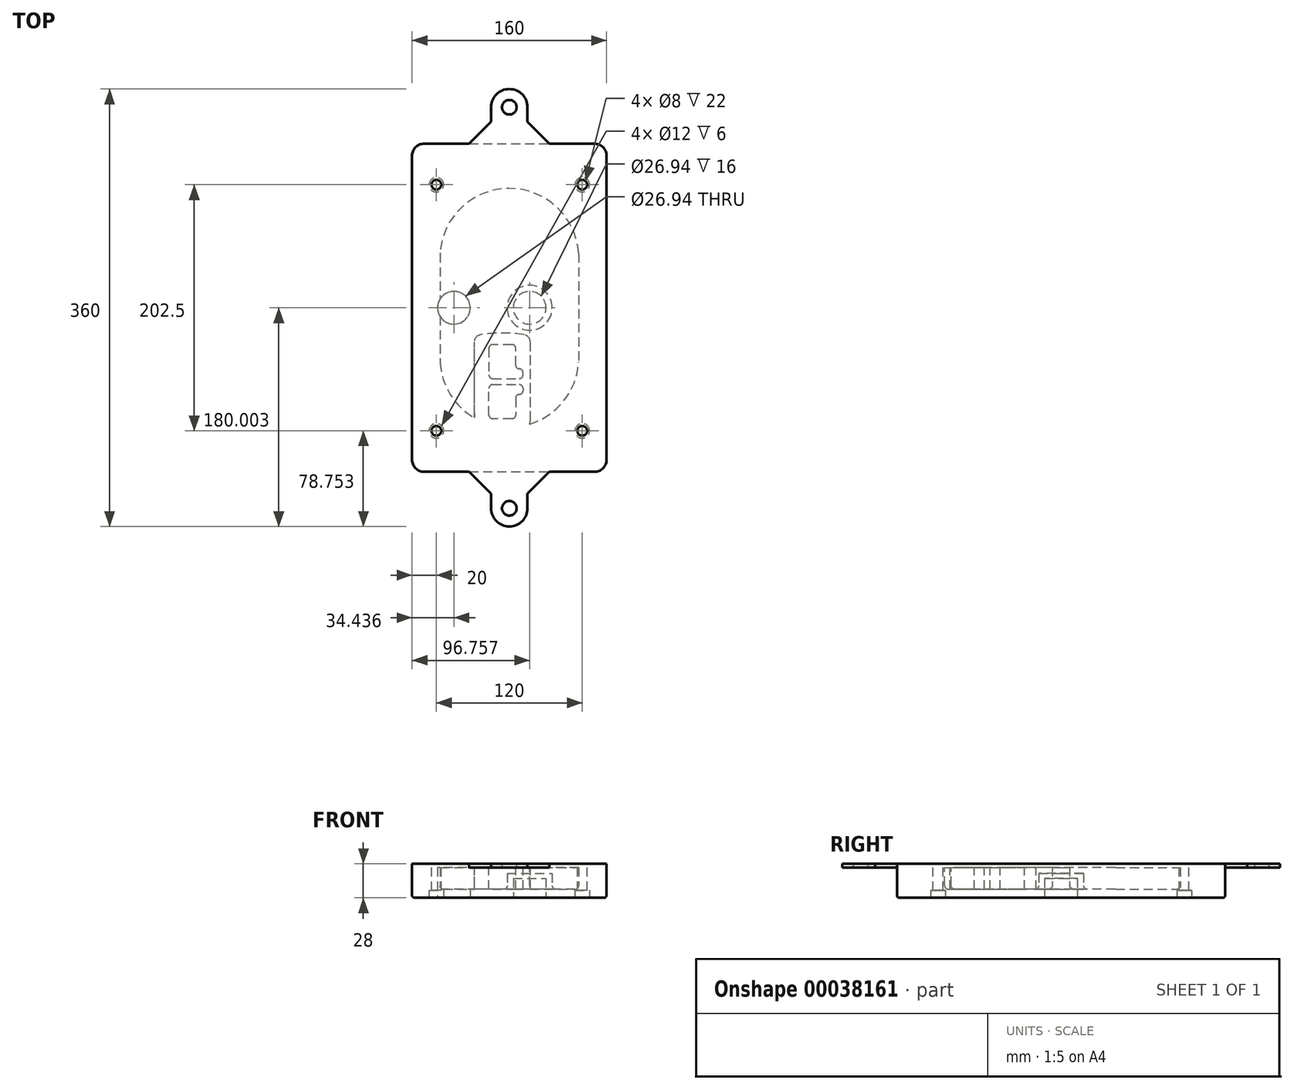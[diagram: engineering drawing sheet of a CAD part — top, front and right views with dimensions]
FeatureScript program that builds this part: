
annotation { "Feature Type Name" : "Feature", "Feature Type Description" : "" }
export const myFeature = defineFeature(function(context is Context, id is Id, definition is map)
    precondition{}
    {
        {
            var Q0;
            Q0=qCreatedBy(makeId("Top.planeOp"),FACE);
            var sketch = newSketch(context, id + "F0", { "sketchPlane" : qUnion([Q0])});
            skPoint(sketch, "E0.rect.middle", {"position": v(0, 0) * mm});
            skLineSegment(sketch, "E1.bottom", {"start": v(24.05, 28.38) * mm, "end": v(164.05, 28.38) * mm});
            skLineSegment(sketch, "E1.top", {"start": v(24.05, 298.38) * mm, "end": v(164.05, 298.38) * mm});
            skLineSegment(sketch, "E1.left", {"start": v(14.05, 38.38) * mm, "end": v(14.05, 288.38) * mm});
            skLineSegment(sketch, "E1.right", {"start": v(174.05, 38.38) * mm, "end": v(174.05, 288.38) * mm});
            skLineSegment(sketch, "E2", {"start": v(14.05, 298.38) * mm, "end": v(174.05, 28.38) * mm, "construction": true});
            skLineSegment(sketch, "E3", {"start": v(174.05, 298.38) * mm, "end": v(14.05, 28.38) * mm, "construction": true});
            skCircle(sketch, "E4", {"center": v(34.05, 264.63) * mm, "radius": 4 * mm});
            skCircle(sketch, "E5", {"center": v(154.05, 264.63) * mm, "radius": 4 * mm});
            skCircle(sketch, "E6", {"center": v(154.05, 62.13) * mm, "radius": 4 * mm});
            skCircle(sketch, "E7", {"center": v(34.05, 62.13) * mm, "radius": 4 * mm});
            skLineSegment(sketch, "E8", {"start": v(34.05, 264.63) * mm, "end": v(154.05, 264.63) * mm, "construction": true});
            skLineSegment(sketch, "E9", {"start": v(154.05, 264.63) * mm, "end": v(154.05, 62.13) * mm, "construction": true});
            skLineSegment(sketch, "E10", {"start": v(154.05, 62.13) * mm, "end": v(34.05, 62.13) * mm, "construction": true});
            skLineSegment(sketch, "E11", {"start": v(34.05, 62.13) * mm, "end": v(34.05, 264.63) * mm, "construction": true});
            skLineSegment(sketch, "E12", {"start": v(34.05, 208.05) * mm, "end": v(34.05, 118.72) * mm});
            skLineSegment(sketch, "E13", {"start": v(154.05, 208.05) * mm, "end": v(154.05, 118.72) * mm});
            skArc(sketch, "E14", {"start": v(154.03, 208.75) * mm, "mid": v(94.05, 264.63) * mm, "end": v(34.07, 208.75) * mm});
            skArc(sketch, "E15", {"start": v(34.07, 118.01) * mm, "mid": v(94.05, 62.13) * mm, "end": v(154.03, 118.01) * mm});
            skLineSegment(sketch, "E16", {"start": v(34.05, 163.38) * mm, "end": v(154.05, 163.38) * mm, "construction": true});
            skPoint(sketch, "E17.visualSharp", {"position": v(34.05, 118.38) * mm});
            skArc(sketch, "E17.filletArc", {"start": v(34.05, 118.72) * mm, "mid": v(34.06, 118.37) * mm, "end": v(34.07, 118.01) * mm});
            skPoint(sketch, "E18.visualSharp", {"position": v(34.05, 208.38) * mm});
            skArc(sketch, "E18.filletArc", {"start": v(34.07, 208.75) * mm, "mid": v(34.06, 208.4) * mm, "end": v(34.05, 208.05) * mm});
            skPoint(sketch, "E19.visualSharp", {"position": v(154.05, 208.38) * mm});
            skArc(sketch, "E19.filletArc", {"start": v(154.05, 208.05) * mm, "mid": v(154.04, 208.4) * mm, "end": v(154.03, 208.75) * mm});
            skPoint(sketch, "E20.visualSharp", {"position": v(154.05, 118.38) * mm});
            skArc(sketch, "E20.filletArc", {"start": v(154.03, 118.01) * mm, "mid": v(154.04, 118.37) * mm, "end": v(154.05, 118.72) * mm});
            skPoint(sketch, "E21.visualSharp", {"position": v(14.05, 298.38) * mm});
            skArc(sketch, "E21.filletArc", {"start": v(24.05, 298.38) * mm, "mid": v(16.98, 295.45) * mm, "end": v(14.05, 288.38) * mm});
            skPoint(sketch, "E22.visualSharp", {"position": v(174.05, 298.38) * mm});
            skArc(sketch, "E22.filletArc", {"start": v(174.05, 288.38) * mm, "mid": v(171.12, 295.45) * mm, "end": v(164.05, 298.38) * mm});
            skPoint(sketch, "E23.visualSharp", {"position": v(174.05, 28.38) * mm});
            skArc(sketch, "E23.filletArc", {"start": v(164.05, 28.38) * mm, "mid": v(171.12, 31.31) * mm, "end": v(174.05, 38.38) * mm});
            skPoint(sketch, "E24.visualSharp", {"position": v(14.05, 28.38) * mm});
            skArc(sketch, "E24.filletArc", {"start": v(14.05, 38.38) * mm, "mid": v(16.98, 31.31) * mm, "end": v(24.05, 28.38) * mm});
            skArc(sketch, "E25.0", {"start": v(151.05, 208.05) * mm, "mid": v(151.05, 208.3) * mm, "end": v(151.03, 208.54) * mm});
            skLineSegment(sketch, "E25.1", {"start": v(151.05, 208.05) * mm, "end": v(151.05, 118.72) * mm});
            skArc(sketch, "E25.2", {"start": v(151.03, 118.23) * mm, "mid": v(151.05, 118.47) * mm, "end": v(151.05, 118.72) * mm});
            skArc(sketch, "E25.3", {"start": v(37.07, 118.23) * mm, "mid": v(94.05, 65.13) * mm, "end": v(151.03, 118.23) * mm});
            skArc(sketch, "E25.4", {"start": v(37.05, 118.72) * mm, "mid": v(37.05, 118.47) * mm, "end": v(37.07, 118.23) * mm});
            skArc(sketch, "E25.5", {"start": v(151.03, 208.54) * mm, "mid": v(94.05, 261.63) * mm, "end": v(37.07, 208.54) * mm});
            skLineSegment(sketch, "E25.6", {"start": v(37.05, 208.05) * mm, "end": v(37.05, 118.72) * mm});
            skArc(sketch, "E25.7", {"start": v(37.07, 208.54) * mm, "mid": v(37.05, 208.3) * mm, "end": v(37.05, 208.05) * mm});
            skArc(sketch, "E26.0", {"start": v(30.08, 209.03) * mm, "mid": v(30.06, 208.54) * mm, "end": v(30.05, 208.05) * mm});
            skArc(sketch, "E26.1", {"start": v(158.02, 209.03) * mm, "mid": v(94.05, 268.63) * mm, "end": v(30.08, 209.03) * mm});
            skArc(sketch, "E26.2", {"start": v(158.05, 208.05) * mm, "mid": v(158.04, 208.54) * mm, "end": v(158.02, 209.03) * mm});
            skLineSegment(sketch, "E26.3", {"start": v(158.05, 208.05) * mm, "end": v(158.05, 118.72) * mm});
            skArc(sketch, "E26.4", {"start": v(158.02, 117.73) * mm, "mid": v(158.04, 118.23) * mm, "end": v(158.05, 118.72) * mm});
            skLineSegment(sketch, "E26.5", {"start": v(30.05, 208.05) * mm, "end": v(30.05, 118.72) * mm});
            skArc(sketch, "E26.6", {"start": v(30.08, 117.73) * mm, "mid": v(94.05, 58.13) * mm, "end": v(158.02, 117.73) * mm});
            skArc(sketch, "E26.7", {"start": v(30.05, 118.72) * mm, "mid": v(30.06, 118.23) * mm, "end": v(30.08, 117.73) * mm});
            skSolve(sketch);
        }
        {
            var Q0;
            Q0=makeQuery(id+"F0.imprint","IMPRINT",FACE,{"disambiguationData":[TD([[makeQuery(id+"F0.imprint","IMPRINT",EDGE,{"derivedFrom":sQuery(id+"F0.wireOp",EDGE,"E1.bottom")}),1.0]])]});
            var Q1;
            Q1=makeQuery(id+"F0.imprint","IMPRINT",FACE,{"disambiguationData":[TD([[makeQuery(id+"F0.imprint","IMPRINT",EDGE,{"derivedFrom":sQuery(id+"F0.wireOp",EDGE,"E12")}),1.0]])]});
            var Q2;
            Q2=makeQuery(id+"F0.imprint","IMPRINT",FACE,{"disambiguationData":[TD([[makeQuery(id+"F0.imprint","IMPRINT",EDGE,{"derivedFrom":sQuery(id+"F0.wireOp",EDGE,"E25.0")}),1.0]])]});
            var Q3;
            Q3=makeQuery(id+"F0.imprint","IMPRINT",FACE,{"disambiguationData":[TD([[makeQuery(id+"F0.imprint","IMPRINT",EDGE,{"derivedFrom":sQuery(id+"F0.wireOp",EDGE,"E12")}),-1.0]])]});
            extrude(context, id + "F1", {"entities" : qUnion([Q0, Q1, Q2, Q3]), "oppositeDirection" : true, "depth" : 25 * mm});
        }
        {
            var Q0;
            Q0=makeQuery(id+"F0.imprint","IMPRINT",FACE,{"disambiguationData":[TD([[makeQuery(id+"F0.imprint","IMPRINT",EDGE,{"derivedFrom":sQuery(id+"F0.wireOp",EDGE,"E12")}),1.0]])]});
            extrude(context, id + "F2", {"entities" : qUnion([Q0]), "operationType" : NewBodyOperationType.ADD, "depth" : 3 * mm});
        }
        {
            var Q0;
            Q0=makeQuery(id+"F0.imprint","IMPRINT",FACE,{"disambiguationData":[TD([[makeQuery(id+"F0.imprint","IMPRINT",EDGE,{"derivedFrom":sQuery(id+"F0.wireOp",EDGE,"E25.0")}),1.0]])]});
            extrude(context, id + "F3", {"entities" : qUnion([Q0]), "operationType" : NewBodyOperationType.REMOVE, "oppositeDirection" : true, "depth" : 18 * mm});
        }
        {
            var Q0;
            Q0=makeQuery(id+"F2.opExtrude","CAP_FACE",FACE,{"disambiguationData":[OSD([sQuery(id+"F0.wireOp",EDGE,"E12"),sQuery(id+"F0.wireOp",EDGE,"E13"),sQuery(id+"F0.wireOp",EDGE,"E14"),sQuery(id+"F0.wireOp",EDGE,"E15"),sQuery(id+"F0.wireOp",EDGE,"E17.filletArc"),sQuery(id+"F0.wireOp",EDGE,"E18.filletArc"),sQuery(id+"F0.wireOp",EDGE,"E19.filletArc"),sQuery(id+"F0.wireOp",EDGE,"E20.filletArc"),sQuery(id+"F0.wireOp",EDGE,"E25.0"),sQuery(id+"F0.wireOp",EDGE,"E25.1"),sQuery(id+"F0.wireOp",EDGE,"E25.2"),sQuery(id+"F0.wireOp",EDGE,"E25.3"),sQuery(id+"F0.wireOp",EDGE,"E25.4"),sQuery(id+"F0.wireOp",EDGE,"E25.5"),sQuery(id+"F0.wireOp",EDGE,"E25.6"),sQuery(id+"F0.wireOp",EDGE,"E25.7")])],"isStart":false});
            var sketch = newSketch(context, id + "F4", { "sketchPlane" : qUnion([Q0])});
            skArc(sketch, "E27.0", {"start": v(69.96, 62.18) * mm, "mid": v(88.3, 60.63) * mm, "end": v(106.64, 62.18) * mm});
            skArc(sketch, "E28.0", {"start": v(106.64, 143.09) * mm, "mid": v(88.3, 144.63) * mm, "end": v(69.96, 143.09) * mm});
            skLineSegment(sketch, "E29", {"start": v(63.3, 135.2) * mm, "end": v(63.3, 70.07) * mm});
            skLineSegment(sketch, "E30", {"start": v(113.3, 135.2) * mm, "end": v(113.3, 70.07) * mm});
            skLineSegment(sketch, "E31", {"start": v(63.3, 141.74) * mm, "end": v(113.3, 141.74) * mm, "construction": true});
            skLineSegment(sketch, "E32", {"start": v(63.3, 63.52) * mm, "end": v(113.3, 63.52) * mm, "construction": true});
            skPoint(sketch, "E33.visualSharp", {"position": v(63.3, 141.74) * mm});
            skArc(sketch, "E33.filletArc", {"start": v(69.96, 143.09) * mm, "mid": v(65.19, 140.36) * mm, "end": v(63.3, 135.2) * mm});
            skPoint(sketch, "E34.visualSharp", {"position": v(113.3, 141.74) * mm});
            skArc(sketch, "E34.filletArc", {"start": v(113.3, 135.2) * mm, "mid": v(111.41, 140.36) * mm, "end": v(106.64, 143.09) * mm});
            skPoint(sketch, "E35.visualSharp", {"position": v(113.3, 63.52) * mm});
            skArc(sketch, "E35.filletArc", {"start": v(106.64, 62.18) * mm, "mid": v(111.41, 64.9) * mm, "end": v(113.3, 70.07) * mm});
            skPoint(sketch, "E36.visualSharp", {"position": v(63.3, 63.52) * mm});
            skArc(sketch, "E36.filletArc", {"start": v(63.3, 70.07) * mm, "mid": v(65.19, 64.9) * mm, "end": v(69.96, 62.18) * mm});
            skArc(sketch, "E37.0", {"start": v(151.03, 208.54) * mm, "mid": v(94.05, 261.63) * mm, "end": v(37.07, 208.54) * mm});
            skArc(sketch, "E37.1", {"start": v(37.07, 208.54) * mm, "mid": v(37.05, 208.3) * mm, "end": v(37.05, 208.05) * mm});
            skLineSegment(sketch, "E37.2", {"start": v(37.05, 208.05) * mm, "end": v(37.05, 118.72) * mm});
            skArc(sketch, "E37.3", {"start": v(37.05, 118.72) * mm, "mid": v(37.05, 118.47) * mm, "end": v(37.07, 118.23) * mm});
            skArc(sketch, "E37.4", {"start": v(37.07, 118.23) * mm, "mid": v(94.05, 65.13) * mm, "end": v(151.03, 118.23) * mm});
            skArc(sketch, "E37.5", {"start": v(151.03, 118.23) * mm, "mid": v(151.05, 118.47) * mm, "end": v(151.05, 118.72) * mm});
            skLineSegment(sketch, "E37.6", {"start": v(151.05, 208.05) * mm, "end": v(151.05, 118.72) * mm});
            skArc(sketch, "E37.7", {"start": v(151.05, 208.05) * mm, "mid": v(151.05, 208.3) * mm, "end": v(151.03, 208.54) * mm});
            skLineSegment(sketch, "E38.0", {"start": v(111.3, 135.2) * mm, "end": v(111.3, 70.07) * mm});
            skArc(sketch, "E38.1", {"start": v(106.3, 64.15) * mm, "mid": v(109.88, 66.2) * mm, "end": v(111.3, 70.07) * mm});
            skArc(sketch, "E38.2", {"start": v(70.3, 64.15) * mm, "mid": v(88.3, 62.63) * mm, "end": v(106.3, 64.15) * mm});
            skArc(sketch, "E38.3", {"start": v(65.3, 70.07) * mm, "mid": v(66.72, 66.2) * mm, "end": v(70.3, 64.15) * mm});
            skLineSegment(sketch, "E38.4", {"start": v(65.3, 135.2) * mm, "end": v(65.3, 70.07) * mm});
            skArc(sketch, "E38.5", {"start": v(111.3, 135.2) * mm, "mid": v(109.88, 139.07) * mm, "end": v(106.3, 141.11) * mm});
            skArc(sketch, "E38.6", {"start": v(70.3, 141.11) * mm, "mid": v(66.72, 139.07) * mm, "end": v(65.3, 135.2) * mm});
            skArc(sketch, "E38.7", {"start": v(106.3, 141.11) * mm, "mid": v(88.3, 142.63) * mm, "end": v(70.3, 141.11) * mm});
            skArc(sketch, "E39.0", {"start": v(109.3, 135.2) * mm, "mid": v(108.36, 137.78) * mm, "end": v(105.97, 139.14) * mm});
            skLineSegment(sketch, "E39.1", {"start": v(109.3, 135.2) * mm, "end": v(109.3, 70.07) * mm});
            skArc(sketch, "E39.2", {"start": v(105.97, 66.12) * mm, "mid": v(108.36, 67.49) * mm, "end": v(109.3, 70.07) * mm});
            skArc(sketch, "E39.3", {"start": v(70.63, 66.12) * mm, "mid": v(88.3, 64.63) * mm, "end": v(105.97, 66.12) * mm});
            skArc(sketch, "E39.4", {"start": v(67.3, 70.07) * mm, "mid": v(68.24, 67.49) * mm, "end": v(70.63, 66.12) * mm});
            skArc(sketch, "E39.5", {"start": v(105.97, 139.14) * mm, "mid": v(88.3, 140.63) * mm, "end": v(70.63, 139.14) * mm});
            skLineSegment(sketch, "E39.6", {"start": v(67.3, 135.2) * mm, "end": v(67.3, 70.07) * mm});
            skArc(sketch, "E39.7", {"start": v(70.63, 139.14) * mm, "mid": v(68.24, 137.78) * mm, "end": v(67.3, 135.2) * mm});
            skLineSegment(sketch, "E40", {"start": v(63.3, 102.63) * mm, "end": v(113.3, 102.63) * mm, "construction": true});
            skLineSegment(sketch, "E41", {"start": v(77.3, 108.13) * mm, "end": v(77.3, 130.13) * mm});
            skLineSegment(sketch, "E42", {"start": v(80.3, 133.13) * mm, "end": v(96.3, 133.13) * mm});
            skLineSegment(sketch, "E43", {"start": v(99.3, 130.13) * mm, "end": v(99.3, 116.13) * mm});
            skLineSegment(sketch, "E44", {"start": v(102.3, 113.13) * mm, "end": v(102.3, 113.13) * mm});
            skLineSegment(sketch, "E45", {"start": v(105.3, 110.13) * mm, "end": v(105.3, 108.13) * mm});
            skLineSegment(sketch, "E46", {"start": v(102.3, 105.13) * mm, "end": v(80.3, 105.13) * mm});
            skPoint(sketch, "E47.visualSharp", {"position": v(77.3, 133.13) * mm});
            skArc(sketch, "E47.filletArc", {"start": v(80.3, 133.13) * mm, "mid": v(78.18, 132.25) * mm, "end": v(77.3, 130.13) * mm});
            skPoint(sketch, "E48.visualSharp", {"position": v(99.3, 133.13) * mm});
            skArc(sketch, "E48.filletArc", {"start": v(99.3, 130.13) * mm, "mid": v(98.42, 132.25) * mm, "end": v(96.3, 133.13) * mm});
            skPoint(sketch, "E49.visualSharp", {"position": v(99.3, 113.13) * mm});
            skArc(sketch, "E49.filletArc", {"start": v(99.3, 116.13) * mm, "mid": v(100.18, 114.01) * mm, "end": v(102.3, 113.13) * mm});
            skPoint(sketch, "E50.visualSharp", {"position": v(105.3, 113.13) * mm});
            skArc(sketch, "E50.filletArc", {"start": v(105.3, 110.13) * mm, "mid": v(104.42, 112.25) * mm, "end": v(102.3, 113.13) * mm});
            skPoint(sketch, "E51.visualSharp", {"position": v(105.3, 105.13) * mm});
            skArc(sketch, "E51.filletArc", {"start": v(102.3, 105.13) * mm, "mid": v(104.42, 106.01) * mm, "end": v(105.3, 108.13) * mm});
            skPoint(sketch, "E52.visualSharp", {"position": v(77.3, 105.13) * mm});
            skArc(sketch, "E52.filletArc", {"start": v(77.3, 108.13) * mm, "mid": v(78.18, 106.01) * mm, "end": v(80.3, 105.13) * mm});
            skLineSegment(sketch, "E53.0.MirrorCS", {"start": v(102.3, 100.13) * mm, "end": v(80.3, 100.13) * mm});
            skArc(sketch, "E54.0.MirrorCS", {"start": v(77.3, 97.13) * mm, "mid": v(78.18, 99.25) * mm, "end": v(80.3, 100.13) * mm});
            skLineSegment(sketch, "E55.0.MirrorCS", {"start": v(77.3, 97.13) * mm, "end": v(77.3, 75.13) * mm});
            skArc(sketch, "E56.0.MirrorCS", {"start": v(80.3, 72.13) * mm, "mid": v(78.18, 73.01) * mm, "end": v(77.3, 75.13) * mm});
            skLineSegment(sketch, "E57.0.MirrorCS", {"start": v(80.3, 72.13) * mm, "end": v(96.3, 72.13) * mm});
            skArc(sketch, "E58.0.MirrorCS", {"start": v(99.3, 75.13) * mm, "mid": v(98.42, 73.01) * mm, "end": v(96.3, 72.13) * mm});
            skLineSegment(sketch, "E59.0.MirrorCS", {"start": v(99.3, 75.13) * mm, "end": v(99.3, 89.13) * mm});
            skArc(sketch, "E60.0.MirrorCS", {"start": v(99.3, 89.13) * mm, "mid": v(100.18, 91.25) * mm, "end": v(102.3, 92.13) * mm});
            skArc(sketch, "E61.0.MirrorCS", {"start": v(105.3, 95.13) * mm, "mid": v(104.42, 93.01) * mm, "end": v(102.3, 92.13) * mm});
            skLineSegment(sketch, "E62.0.MirrorCS", {"start": v(105.3, 95.13) * mm, "end": v(105.3, 97.13) * mm});
            skArc(sketch, "E63.0.MirrorCS", {"start": v(102.3, 100.13) * mm, "mid": v(104.42, 99.25) * mm, "end": v(105.3, 97.13) * mm});
            skSolve(sketch);
        }
        {
            var Q0;
            Q0=makeQuery(id+"F4.imprint","IMPRINT",FACE,{"disambiguationData":[TD([[makeQuery(id+"F4.imprint","IMPRINT",EDGE,{"derivedFrom":sQuery(id+"F4.wireOp",EDGE,"E27.0")}),1.0]])]});
            var Q1;
            Q1=makeQuery(id+"F4.imprint","IMPRINT",FACE,{"disambiguationData":[TD([[makeQuery(id+"F4.imprint","IMPRINT",EDGE,{"derivedFrom":sQuery(id+"F4.wireOp",EDGE,"E38.0")}),-1.0]])]});
            var Q2;
            Q2=makeQuery(id+"F4.imprint","IMPRINT",FACE,{"disambiguationData":[TD([[makeQuery(id+"F4.imprint","IMPRINT",EDGE,{"derivedFrom":sQuery(id+"F4.wireOp",EDGE,"E39.0")}),1.0]])]});
            extrude(context, id + "F5", {"entities" : qUnion([Q0, Q1, Q2]), "operationType" : NewBodyOperationType.ADD, "endBound" : BoundingType.UP_TO_NEXT, "oppositeDirection" : true, "depth" : 25 * mm});
        }
        {
            var Q0;
            Q0=makeQuery(id+"F4.imprint","IMPRINT",FACE,{"disambiguationData":[TD([[makeQuery(id+"F4.imprint","IMPRINT",EDGE,{"derivedFrom":sQuery(id+"F4.wireOp",EDGE,"E38.0")}),-1.0]])]});
            extrude(context, id + "F6", {"entities" : qUnion([Q0]), "operationType" : NewBodyOperationType.REMOVE, "oppositeDirection" : true, "depth" : 2 * mm});
        }
        {
            var Q0;
            Q0=makeQuery(id+"F1.opExtrude","CAP_FACE",FACE,{"disambiguationData":[OSD([sQuery(id+"F0.wireOp",EDGE,"E1.bottom"),sQuery(id+"F0.wireOp",EDGE,"E1.top"),sQuery(id+"F0.wireOp",EDGE,"E1.left"),sQuery(id+"F0.wireOp",EDGE,"E1.right"),sQuery(id+"F0.wireOp",EDGE,"E4"),sQuery(id+"F0.wireOp",EDGE,"E5"),sQuery(id+"F0.wireOp",EDGE,"E6"),sQuery(id+"F0.wireOp",EDGE,"E7"),sQuery(id+"F0.wireOp",EDGE,"E21.filletArc"),sQuery(id+"F0.wireOp",EDGE,"E22.filletArc"),sQuery(id+"F0.wireOp",EDGE,"E23.filletArc"),sQuery(id+"F0.wireOp",EDGE,"E24.filletArc")])],"isStart":false});
            var sketch = newSketch(context, id + "F7", { "sketchPlane" : qUnion([Q0])});
            skCircle(sketch, "E64", {"center": v(110.8, -163.38) * mm, "radius": 13.47 * mm});
            skCircle(sketch, "E65", {"center": v(48.49, -163.38) * mm, "radius": 13.47 * mm});
            skLineSegment(sketch, "E66", {"start": v(174.05, -163.38) * mm, "end": v(14.05, -163.38) * mm});
            skCircle(sketch, "E67", {"center": v(110.8, -163.38) * mm, "radius": 18.47 * mm});
            skCircle(sketch, "E68", {"center": v(154.05, -264.63) * mm, "radius": 6 * mm});
            skCircle(sketch, "E69", {"center": v(34.05, -264.63) * mm, "radius": 6 * mm});
            skCircle(sketch, "E70", {"center": v(34.05, -62.13) * mm, "radius": 6 * mm});
            skCircle(sketch, "E71", {"center": v(154.05, -62.13) * mm, "radius": 6 * mm});
            skSolve(sketch);
        }
        {
            var Q0;
            {var subQ1=sQuery(id+"F7.wireOp",EDGE,"E66");var subQ4=sQuery(id+"F7.wireOp",EDGE,"E64");var subQ6=makeQuery(id+"F7.imprint","INTERSECT",VERTEX,{"disambiguationData":[OD(0.0)],"derivedFrom":[subQ4,subQ1]});Q0=makeQuery(id+"F7.imprint","IMPRINT",FACE,{"disambiguationData":[TD([[makeQuery(id+"F7.imprint","IMPRINT",EDGE,{"disambiguationData":[TD([[subQ6,-1.0]])],"derivedFrom":subQ4}),-1.0]])]});}
            var Q1;
            {var subQ0=sQuery(id+"F7.wireOp",EDGE,"E66");var subQ1=sQuery(id+"F7.wireOp",EDGE,"E64");var subQ3=makeQuery(id+"F7.imprint","INTERSECT",VERTEX,{"disambiguationData":[OD(0.0)],"derivedFrom":[subQ1,subQ0]});Q1=makeQuery(id+"F7.imprint","IMPRINT",FACE,{"disambiguationData":[TD([[makeQuery(id+"F7.imprint","IMPRINT",EDGE,{"disambiguationData":[TD([[subQ3,-1.0]])],"derivedFrom":subQ1}),1.0]])]});}
            var Q2;
            {var subQ0=sQuery(id+"F7.wireOp",EDGE,"E66");var subQ1=sQuery(id+"F7.wireOp",EDGE,"E64");var subQ3=makeQuery(id+"F7.imprint","INTERSECT",VERTEX,{"disambiguationData":[OD(0.0)],"derivedFrom":[subQ1,subQ0]});Q2=makeQuery(id+"F7.imprint","IMPRINT",FACE,{"disambiguationData":[TD([[makeQuery(id+"F7.imprint","IMPRINT",EDGE,{"disambiguationData":[TD([[subQ3,1.0]])],"derivedFrom":subQ1}),1.0]])]});}
            var Q3;
            {var subQ1=sQuery(id+"F7.wireOp",EDGE,"E66");var subQ4=sQuery(id+"F7.wireOp",EDGE,"E64");var subQ6=makeQuery(id+"F7.imprint","INTERSECT",VERTEX,{"disambiguationData":[OD(0.0)],"derivedFrom":[subQ4,subQ1]});Q3=makeQuery(id+"F7.imprint","IMPRINT",FACE,{"disambiguationData":[TD([[makeQuery(id+"F7.imprint","IMPRINT",EDGE,{"disambiguationData":[TD([[subQ6,1.0]])],"derivedFrom":subQ4}),-1.0]])]});}
            extrude(context, id + "F8", {"entities" : qUnion([Q0, Q1, Q2, Q3]), "operationType" : NewBodyOperationType.ADD, "oppositeDirection" : true, "depth" : 20 * mm});
        }
        {
            var Q0;
            {var subQ0=sQuery(id+"F7.wireOp",EDGE,"E66");var subQ1=sQuery(id+"F7.wireOp",EDGE,"E64");var subQ3=makeQuery(id+"F7.imprint","INTERSECT",VERTEX,{"disambiguationData":[OD(0.0)],"derivedFrom":[subQ1,subQ0]});Q0=makeQuery(id+"F7.imprint","IMPRINT",FACE,{"disambiguationData":[TD([[makeQuery(id+"F7.imprint","IMPRINT",EDGE,{"disambiguationData":[TD([[subQ3,-1.0]])],"derivedFrom":subQ1}),1.0]])]});}
            var Q1;
            {var subQ0=sQuery(id+"F7.wireOp",EDGE,"E66");var subQ1=sQuery(id+"F7.wireOp",EDGE,"E64");var subQ3=makeQuery(id+"F7.imprint","INTERSECT",VERTEX,{"disambiguationData":[OD(0.0)],"derivedFrom":[subQ1,subQ0]});Q1=makeQuery(id+"F7.imprint","IMPRINT",FACE,{"disambiguationData":[TD([[makeQuery(id+"F7.imprint","IMPRINT",EDGE,{"disambiguationData":[TD([[subQ3,1.0]])],"derivedFrom":subQ1}),1.0]])]});}
            extrude(context, id + "F9", {"entities" : qUnion([Q0, Q1]), "operationType" : NewBodyOperationType.REMOVE, "oppositeDirection" : true, "depth" : 16 * mm});
        }
        {
            var Q0;
            {var subQ0=sQuery(id+"F7.wireOp",EDGE,"E66");var subQ1=sQuery(id+"F7.wireOp",EDGE,"E65");var subQ3=makeQuery(id+"F7.imprint","INTERSECT",VERTEX,{"disambiguationData":[OD(0.0)],"derivedFrom":[subQ1,subQ0]});Q0=makeQuery(id+"F7.imprint","IMPRINT",FACE,{"disambiguationData":[TD([[makeQuery(id+"F7.imprint","IMPRINT",EDGE,{"disambiguationData":[TD([[subQ3,-1.0]])],"derivedFrom":subQ1}),1.0]])]});}
            var Q1;
            {var subQ0=sQuery(id+"F7.wireOp",EDGE,"E66");var subQ1=sQuery(id+"F7.wireOp",EDGE,"E65");var subQ3=makeQuery(id+"F7.imprint","INTERSECT",VERTEX,{"disambiguationData":[OD(0.0)],"derivedFrom":[subQ1,subQ0]});Q1=makeQuery(id+"F7.imprint","IMPRINT",FACE,{"disambiguationData":[TD([[makeQuery(id+"F7.imprint","IMPRINT",EDGE,{"disambiguationData":[TD([[subQ3,1.0]])],"derivedFrom":subQ1}),1.0]])]});}
            extrude(context, id + "F10", {"entities" : qUnion([Q0, Q1]), "operationType" : NewBodyOperationType.REMOVE, "oppositeDirection" : true, "depth" : 25 * mm});
        }
        {
            var Q0;
            Q0=makeQuery(id+"F7.imprint","IMPRINT",FACE,{"disambiguationData":[TD([[makeQuery(id+"F7.imprint","IMPRINT",EDGE,{"derivedFrom":sQuery(id+"F7.wireOp",EDGE,"E68")}),1.0]])]});
            var Q1;
            Q1=makeQuery(id+"F7.imprint","IMPRINT",FACE,{"disambiguationData":[TD([[makeQuery(id+"F7.imprint","IMPRINT",EDGE,{"derivedFrom":makeQuery(id+"F1.opExtrude","CAP_EDGE",EDGE,{"disambiguationData":[OSD([sQuery(id+"F0.wireOp",EDGE,"E5")])],"isStart":false})}),-1.0]])]});
            var Q2;
            Q2=makeQuery(id+"F7.imprint","IMPRINT",FACE,{"disambiguationData":[TD([[makeQuery(id+"F7.imprint","IMPRINT",EDGE,{"derivedFrom":sQuery(id+"F7.wireOp",EDGE,"E69")}),1.0]])]});
            var Q3;
            Q3=makeQuery(id+"F7.imprint","IMPRINT",FACE,{"disambiguationData":[TD([[makeQuery(id+"F7.imprint","IMPRINT",EDGE,{"derivedFrom":makeQuery(id+"F1.opExtrude","CAP_EDGE",EDGE,{"disambiguationData":[OSD([sQuery(id+"F0.wireOp",EDGE,"E4")])],"isStart":false})}),-1.0]])]});
            var Q4;
            Q4=makeQuery(id+"F7.imprint","IMPRINT",FACE,{"disambiguationData":[TD([[makeQuery(id+"F7.imprint","IMPRINT",EDGE,{"derivedFrom":sQuery(id+"F7.wireOp",EDGE,"E70")}),1.0]])]});
            var Q5;
            Q5=makeQuery(id+"F7.imprint","IMPRINT",FACE,{"disambiguationData":[TD([[makeQuery(id+"F7.imprint","IMPRINT",EDGE,{"derivedFrom":makeQuery(id+"F1.opExtrude","CAP_EDGE",EDGE,{"disambiguationData":[OSD([sQuery(id+"F0.wireOp",EDGE,"E7")])],"isStart":false})}),-1.0]])]});
            var Q6;
            Q6=makeQuery(id+"F7.imprint","IMPRINT",FACE,{"disambiguationData":[TD([[makeQuery(id+"F7.imprint","IMPRINT",EDGE,{"derivedFrom":sQuery(id+"F7.wireOp",EDGE,"E71")}),1.0]])]});
            var Q7;
            Q7=makeQuery(id+"F7.imprint","IMPRINT",FACE,{"disambiguationData":[TD([[makeQuery(id+"F7.imprint","IMPRINT",EDGE,{"derivedFrom":makeQuery(id+"F1.opExtrude","CAP_EDGE",EDGE,{"disambiguationData":[OSD([sQuery(id+"F0.wireOp",EDGE,"E6")])],"isStart":false})}),-1.0]])]});
            extrude(context, id + "F11", {"entities" : qUnion([Q0, Q1, Q2, Q3, Q4, Q5, Q6, Q7]), "operationType" : NewBodyOperationType.REMOVE, "oppositeDirection" : true, "depth" : 6 * mm});
        }
        {
            var Q0;
            Q0=makeQuery(id+"F9.boolean.opBoolean","COPY",FACE,{"derivedFrom":makeQuery(id+"F9.opExtrude","CAP_FACE",FACE,{"disambiguationData":[OSD([sQuery(id+"F7.wireOp",EDGE,"E64")])],"isStart":false})});
            var sketch = newSketch(context, id + "F12", { "sketchPlane" : qUnion([Q0])});
            skArc(sketch, "E72.0", {"start": v(99.3, -148.94) * mm, "mid": v(119.29, -179.79) * mm, "end": v(105.67, -145.64) * mm});
            skArc(sketch, "E72.1", {"start": v(105.27, -145.76) * mm, "mid": v(102.14, -147.07) * mm, "end": v(99.3, -148.94) * mm});
            skLineSegment(sketch, "E73", {"start": v(92.5, -105.13) * mm, "end": v(102.3, -105.13) * mm});
            skLineSegment(sketch, "E74.0", {"start": v(102.3, -100.13) * mm, "end": v(92.5, -100.13) * mm});
            skArc(sketch, "E74.1", {"start": v(102.3, -100.13) * mm, "mid": v(104.42, -99.25) * mm, "end": v(105.3, -97.13) * mm});
            skLineSegment(sketch, "E74.2", {"start": v(105.3, -95.13) * mm, "end": v(105.3, -97.13) * mm});
            skArc(sketch, "E74.3", {"start": v(105.3, -95.13) * mm, "mid": v(104.42, -93.01) * mm, "end": v(102.3, -92.13) * mm});
            skArc(sketch, "E74.4", {"start": v(99.3, -89.13) * mm, "mid": v(100.18, -91.25) * mm, "end": v(102.3, -92.13) * mm});
            skLineSegment(sketch, "E74.5", {"start": v(99.3, -89.13) * mm, "end": v(99.3, -148.94) * mm});
            skLineSegment(sketch, "E74.7", {"start": v(102.3, -105.13) * mm, "end": v(92.5, -105.13) * mm});
            skArc(sketch, "E74.8", {"start": v(102.3, -105.13) * mm, "mid": v(104.42, -106.01) * mm, "end": v(105.3, -108.13) * mm});
            skLineSegment(sketch, "E74.9", {"start": v(105.3, -110.13) * mm, "end": v(105.3, -108.13) * mm});
            skArc(sketch, "E74.10", {"start": v(105.3, -110.13) * mm, "mid": v(104.42, -112.25) * mm, "end": v(102.3, -113.13) * mm});
            skArc(sketch, "E74.11", {"start": v(99.3, -116.13) * mm, "mid": v(100.18, -114.01) * mm, "end": v(102.3, -113.13) * mm});
            skLineSegment(sketch, "E74.12", {"start": v(99.3, -148.94) * mm, "end": v(99.3, -116.13) * mm});
            skPoint(sketch, "E75.orphan", {"position": v(99.3, -130.13) * mm});
            skPoint(sketch, "E76.orphan", {"position": v(80.3, -105.13) * mm});
            skPoint(sketch, "E77.orphan", {"position": v(80.3, -100.13) * mm});
            skPoint(sketch, "E78.orphan", {"position": v(99.3, -75.13) * mm});
            skSolve(sketch);
        }
        {
            var Q0;
            {var subQ7=sQuery(id+"F12.wireOp",EDGE,"E72.0");var subQ14=sQuery(id+"F12.wireOp",EDGE,"E72.1");var subQ16=sQuery(id+"F12.wireOp",EDGE,"E74.1");var subQ18=sQuery(id+"F12.wireOp",EDGE,"E74.8");Q0=qUnion([makeQuery(id+"F12.imprint","IMPRINT",FACE,{"disambiguationData":[TD([[makeQuery(id+"F12.imprint","IMPRINT",EDGE,{"derivedFrom":subQ7}),1.0]])]}),makeQuery(id+"F12.imprint","IMPRINT",FACE,{"disambiguationData":[TD([[makeQuery(id+"F12.imprint","IMPRINT",EDGE,{"derivedFrom":subQ14}),1.0]])]}),makeQuery(id+"F12.imprint","IMPRINT",FACE,{"disambiguationData":[TD([[makeQuery(id+"F12.imprint","IMPRINT",EDGE,{"derivedFrom":subQ16}),1.0]])]}),makeQuery(id+"F12.imprint","IMPRINT",FACE,{"disambiguationData":[TD([[makeQuery(id+"F12.imprint","IMPRINT",EDGE,{"derivedFrom":subQ18}),-1.0]])]})]);}
            var Q1;
            Q1=makeQuery(id+"F5.boolean.opBoolean","SPLIT",FACE,{"disambiguationData":[TD([makeQuery(id+"F5.opExtrude","SWEPT_FACE",FACE,{"disambiguationData":[OSD([sQuery(id+"F4.wireOp",EDGE,"E41")])]})])],"derivedFrom":makeQuery(id+"F3.boolean.opBoolean","COPY",FACE,{"derivedFrom":makeQuery(id+"F3.opExtrude","CAP_FACE",FACE,{"disambiguationData":[OSD([sQuery(id+"F0.wireOp",EDGE,"E25.0"),sQuery(id+"F0.wireOp",EDGE,"E25.1"),sQuery(id+"F0.wireOp",EDGE,"E25.2"),sQuery(id+"F0.wireOp",EDGE,"E25.3"),sQuery(id+"F0.wireOp",EDGE,"E25.4"),sQuery(id+"F0.wireOp",EDGE,"E25.5"),sQuery(id+"F0.wireOp",EDGE,"E25.6"),sQuery(id+"F0.wireOp",EDGE,"E25.7")])],"isStart":false})})});
            extrude(context, id + "F13", {"entities" : qUnion([Q0]), "operationType" : NewBodyOperationType.REMOVE, "endBound" : BoundingType.UP_TO_SURFACE, "endBoundEntityFace" : qUnion([Q1]), "depth" : 25 * mm});
        }
        {
            var Q0;
            Q0=makeQuery(id+"F3.boolean.opBoolean","COPY",EDGE,{"derivedFrom":makeQuery(id+"F3.opExtrude","CAP_EDGE",EDGE,{"disambiguationData":[OSD([sQuery(id+"F0.wireOp",EDGE,"E25.6")])],"isStart":false})});
            var Q1;
            Q1=makeQuery(id+"F8.boolean.opBoolean","INTERSECT",EDGE,{"derivedFrom":[makeQuery(id+"F5.opExtrude","SWEPT_FACE",FACE,{"disambiguationData":[OSD([sQuery(id+"F4.wireOp",EDGE,"E30")])]}),makeQuery(id+"F8.opExtrude","CAP_FACE",FACE,{"disambiguationData":[OSD([sQuery(id+"F7.wireOp",EDGE,"E67")])],"isStart":false})]});
            var Q2;
            Q2=makeQuery(id+"F8.boolean.opBoolean","INTERSECT",EDGE,{"disambiguationData":[OD(1.0)],"derivedFrom":[makeQuery(id+"F5.opExtrude","SWEPT_FACE",FACE,{"disambiguationData":[OSD([sQuery(id+"F4.wireOp",EDGE,"E30")])]}),makeQuery(id+"F8.opExtrude","SWEPT_FACE",FACE,{"disambiguationData":[OSD([sQuery(id+"F7.wireOp",EDGE,"E67")])]})]});
            var Q3;
            {var subQ0=makeQuery(id+"F3.boolean.opBoolean","COPY",FACE,{"derivedFrom":makeQuery(id+"F3.opExtrude","CAP_FACE",FACE,{"disambiguationData":[OSD([sQuery(id+"F0.wireOp",EDGE,"E25.0"),sQuery(id+"F0.wireOp",EDGE,"E25.1"),sQuery(id+"F0.wireOp",EDGE,"E25.2"),sQuery(id+"F0.wireOp",EDGE,"E25.3"),sQuery(id+"F0.wireOp",EDGE,"E25.4"),sQuery(id+"F0.wireOp",EDGE,"E25.5"),sQuery(id+"F0.wireOp",EDGE,"E25.6"),sQuery(id+"F0.wireOp",EDGE,"E25.7")])],"isStart":false})});var subQ1=sQuery(id+"F4.wireOp",EDGE,"E30");Q3=makeQuery(id+"F8.boolean.opBoolean","SPLIT",EDGE,{"disambiguationData":[TD([makeQuery(id+"F5.opExtrude","SWEPT_FACE",FACE,{"disambiguationData":[OSD([sQuery(id+"F4.wireOp",EDGE,"E35.filletArc")])]})])],"derivedFrom":makeQuery(id+"F5.opExtrude","TWEAK_EDGE",EDGE,{"derivedFrom":[subQ0,makeQuery(id+"F4.imprint","IMPRINT",EDGE,{"derivedFrom":subQ1})]})});}
            var Q4;
            {var subQ0=sQuery(id+"F0.wireOp",EDGE,"E25.0");var subQ1=sQuery(id+"F0.wireOp",EDGE,"E25.1");var subQ2=sQuery(id+"F0.wireOp",EDGE,"E25.2");var subQ3=sQuery(id+"F0.wireOp",EDGE,"E25.3");var subQ4=sQuery(id+"F0.wireOp",EDGE,"E25.4");var subQ5=sQuery(id+"F0.wireOp",EDGE,"E25.5");var subQ6=sQuery(id+"F0.wireOp",EDGE,"E25.6");var subQ7=sQuery(id+"F0.wireOp",EDGE,"E25.7");Q4=makeQuery(id+"F8.boolean.opBoolean","INTERSECT",EDGE,{"derivedFrom":[makeQuery(id+"F5.boolean.opBoolean","SPLIT",FACE,{"disambiguationData":[TD([makeQuery(id+"F2.opExtrude","SWEPT_FACE",FACE,{"disambiguationData":[OSD([subQ0])]})])],"derivedFrom":makeQuery(id+"F3.boolean.opBoolean","COPY",FACE,{"derivedFrom":makeQuery(id+"F3.opExtrude","CAP_FACE",FACE,{"disambiguationData":[OSD([subQ0,subQ1,subQ2,subQ3,subQ4,subQ5,subQ6,subQ7])],"isStart":false})})}),makeQuery(id+"F8.opExtrude","SWEPT_FACE",FACE,{"disambiguationData":[OSD([sQuery(id+"F7.wireOp",EDGE,"E67")])]})]});}
            var Q5;
            Q5=makeQuery(id+"F8.boolean.opBoolean","INTERSECT",EDGE,{"disambiguationData":[OD(0.0)],"derivedFrom":[makeQuery(id+"F5.opExtrude","SWEPT_FACE",FACE,{"disambiguationData":[OSD([sQuery(id+"F4.wireOp",EDGE,"E30")])]}),makeQuery(id+"F8.opExtrude","SWEPT_FACE",FACE,{"disambiguationData":[OSD([sQuery(id+"F7.wireOp",EDGE,"E67")])]})]});
            fillet(context, id + "F14", {"entities" : qUnion([Q0, Q1, Q2, Q3, Q4, Q5]), "radius" : 3 * mm, "tangentPropagation" : true, "allowEdgeOverflow" : false});
        }
        {
            var Q0;
            Q0=makeQuery(id+"F1.opExtrude","CAP_EDGE",EDGE,{"disambiguationData":[OSD([sQuery(id+"F0.wireOp",EDGE,"E1.bottom")])],"isStart":false});
            fillet(context, id + "F15", {"entities" : qUnion([Q0]), "radius" : 2 * mm, "tangentPropagation" : true, "allowEdgeOverflow" : false});
        }
        {
            var Q0;
            {var subQ0=sQuery(id+"F0.wireOp",EDGE,"E1.bottom");var subQ1=sQuery(id+"F0.wireOp",EDGE,"E1.top");var subQ2=sQuery(id+"F0.wireOp",EDGE,"E1.left");var subQ3=sQuery(id+"F0.wireOp",EDGE,"E1.right");var subQ4=sQuery(id+"F0.wireOp",EDGE,"E4");var subQ5=sQuery(id+"F0.wireOp",EDGE,"E5");var subQ6=sQuery(id+"F0.wireOp",EDGE,"E6");var subQ7=sQuery(id+"F0.wireOp",EDGE,"E7");var subQ8=sQuery(id+"F0.wireOp",EDGE,"E21.filletArc");var subQ9=sQuery(id+"F0.wireOp",EDGE,"E22.filletArc");var subQ10=sQuery(id+"F0.wireOp",EDGE,"E23.filletArc");var subQ11=sQuery(id+"F0.wireOp",EDGE,"E24.filletArc");Q0=makeQuery(id+"F2.boolean.opBoolean","SPLIT",FACE,{"disambiguationData":[TD([makeQuery(id+"F1.opExtrude","SWEPT_FACE",FACE,{"disambiguationData":[OSD([subQ0])]})])],"derivedFrom":makeQuery(id+"F1.opExtrude","CAP_FACE",FACE,{"disambiguationData":[OSD([subQ0,subQ1,subQ2,subQ3,subQ4,subQ5,subQ6,subQ7,subQ8,subQ9,subQ10,subQ11])],"isStart":true})});}
            var sketch = newSketch(context, id + "F16", { "sketchPlane" : qUnion([Q0])});
            skLineSegment(sketch, "E79.0", {"start": v(24.05, 298.38) * mm, "end": v(164.05, 298.38) * mm});
            skArc(sketch, "E79.1", {"start": v(174.05, 288.38) * mm, "mid": v(171.12, 295.45) * mm, "end": v(164.05, 298.38) * mm});
            skLineSegment(sketch, "E79.2", {"start": v(174.05, 38.38) * mm, "end": v(174.05, 288.38) * mm});
            skArc(sketch, "E79.3", {"start": v(164.05, 28.38) * mm, "mid": v(171.12, 31.31) * mm, "end": v(174.05, 38.38) * mm});
            skLineSegment(sketch, "E79.4", {"start": v(24.05, 28.38) * mm, "end": v(164.05, 28.38) * mm});
            skArc(sketch, "E79.5", {"start": v(14.05, 38.38) * mm, "mid": v(16.98, 31.31) * mm, "end": v(24.05, 28.38) * mm});
            skLineSegment(sketch, "E79.6", {"start": v(14.05, 38.38) * mm, "end": v(14.05, 288.38) * mm});
            skArc(sketch, "E79.7", {"start": v(24.05, 298.38) * mm, "mid": v(16.98, 295.45) * mm, "end": v(14.05, 288.38) * mm});
            skCircle(sketch, "E79.8", {"center": v(34.05, 264.63) * mm, "radius": 4 * mm});
            skCircle(sketch, "E79.9", {"center": v(154.05, 264.63) * mm, "radius": 4 * mm});
            skCircle(sketch, "E79.10", {"center": v(154.05, 62.13) * mm, "radius": 4 * mm});
            skCircle(sketch, "E79.11", {"center": v(34.05, 62.13) * mm, "radius": 4 * mm});
            skArc(sketch, "E79.12", {"start": v(34.07, 118.01) * mm, "mid": v(42.86, 90.71) * mm, "end": v(63.3, 70.6) * mm});
            skArc(sketch, "E79.13", {"start": v(34.05, 118.72) * mm, "mid": v(34.06, 118.37) * mm, "end": v(34.07, 118.01) * mm});
            skLineSegment(sketch, "E79.14", {"start": v(34.05, 208.05) * mm, "end": v(34.05, 118.72) * mm});
            skArc(sketch, "E79.15", {"start": v(34.07, 208.75) * mm, "mid": v(34.06, 208.4) * mm, "end": v(34.05, 208.05) * mm});
            skArc(sketch, "E79.16", {"start": v(154.03, 208.75) * mm, "mid": v(94.05, 264.63) * mm, "end": v(34.07, 208.75) * mm});
            skArc(sketch, "E79.17", {"start": v(154.05, 208.05) * mm, "mid": v(154.04, 208.4) * mm, "end": v(154.03, 208.75) * mm});
            skLineSegment(sketch, "E79.18", {"start": v(154.05, 208.05) * mm, "end": v(154.05, 118.72) * mm});
            skArc(sketch, "E79.19", {"start": v(143.82, 108.72) * mm, "mid": v(151.04, 111.57) * mm, "end": v(154.05, 118.72) * mm});
            skPoint(sketch, "E80.endSnap0", {"position": v(94.05, 298.38) * mm});
            skCircle(sketch, "E81", {"center": v(94.05, 328.38) * mm, "radius": 6 * mm});
            skLineSegment(sketch, "E82", {"start": v(61.05, 298.38) * mm, "end": v(79.05, 316.38) * mm});
            skLineSegment(sketch, "E83", {"start": v(94.05, 298.38) * mm, "end": v(94.05, 328.38) * mm, "construction": true});
            skLineSegment(sketch, "E84", {"start": v(79.05, 316.38) * mm, "end": v(79.05, 328.38) * mm});
            skLineSegment(sketch, "E85", {"start": v(109.05, 316.38) * mm, "end": v(109.05, 328.38) * mm});
            skArc(sketch, "E86", {"start": v(109.05, 328.38) * mm, "mid": v(94.05, 343.38) * mm, "end": v(79.05, 328.38) * mm});
            skLineSegment(sketch, "E87", {"start": v(14.05, 163.38) * mm, "end": v(174.05, 163.38) * mm, "construction": true});
            skPoint(sketch, "E88.MirrorP", {"position": v(94.05, 28.38) * mm});
            skLineSegment(sketch, "E89.MirrorCS", {"start": v(88.3, 176.88) * mm, "end": v(88.3, 206.88) * mm, "construction": true});
            skLineSegment(sketch, "E90", {"start": v(127.05, 298.38) * mm, "end": v(109.05, 316.38) * mm});
            skLineSegment(sketch, "E91.MirrorCS", {"start": v(61.05, 28.38) * mm, "end": v(79.05, 10.38) * mm});
            skLineSegment(sketch, "E92.MirrorCS", {"start": v(79.05, 10.38) * mm, "end": v(79.05, -1.62) * mm});
            skArc(sketch, "E93.MirrorCS", {"start": v(109.05, -1.62) * mm, "mid": v(94.05, -16.62) * mm, "end": v(79.05, -1.62) * mm});
            skLineSegment(sketch, "E94.MirrorCS", {"start": v(109.05, 10.38) * mm, "end": v(109.05, -1.62) * mm});
            skCircle(sketch, "E95.MirrorC", {"center": v(94.05, -1.62) * mm, "radius": 6 * mm});
            skLineSegment(sketch, "E96.MirrorCS", {"start": v(94.05, 28.38) * mm, "end": v(94.05, -1.62) * mm});
            skLineSegment(sketch, "E97.MirrorCS", {"start": v(127.05, 28.38) * mm, "end": v(109.05, 10.38) * mm});
            skSolve(sketch);
        }
        {
            var Q0;
            Q0 = qSketchRegion(id + "F16", true);
            var Q1;
            Q1=makeQuery(id+"F2.opExtrude","CAP_FACE",FACE,{"disambiguationData":[OSD([sQuery(id+"F0.wireOp",EDGE,"E12"),sQuery(id+"F0.wireOp",EDGE,"E13"),sQuery(id+"F0.wireOp",EDGE,"E14"),sQuery(id+"F0.wireOp",EDGE,"E15"),sQuery(id+"F0.wireOp",EDGE,"E17.filletArc"),sQuery(id+"F0.wireOp",EDGE,"E18.filletArc"),sQuery(id+"F0.wireOp",EDGE,"E19.filletArc"),sQuery(id+"F0.wireOp",EDGE,"E20.filletArc"),sQuery(id+"F0.wireOp",EDGE,"E25.0"),sQuery(id+"F0.wireOp",EDGE,"E25.1"),sQuery(id+"F0.wireOp",EDGE,"E25.2"),sQuery(id+"F0.wireOp",EDGE,"E25.3"),sQuery(id+"F0.wireOp",EDGE,"E25.4"),sQuery(id+"F0.wireOp",EDGE,"E25.5"),sQuery(id+"F0.wireOp",EDGE,"E25.6"),sQuery(id+"F0.wireOp",EDGE,"E25.7")])],"isStart":false});
            extrude(context, id + "F17", {"entities" : qUnion([Q0]), "operationType" : NewBodyOperationType.ADD, "endBound" : BoundingType.UP_TO_SURFACE, "endBoundEntityFace" : qUnion([Q1]), "depth" : 25 * mm});
        }
    });
